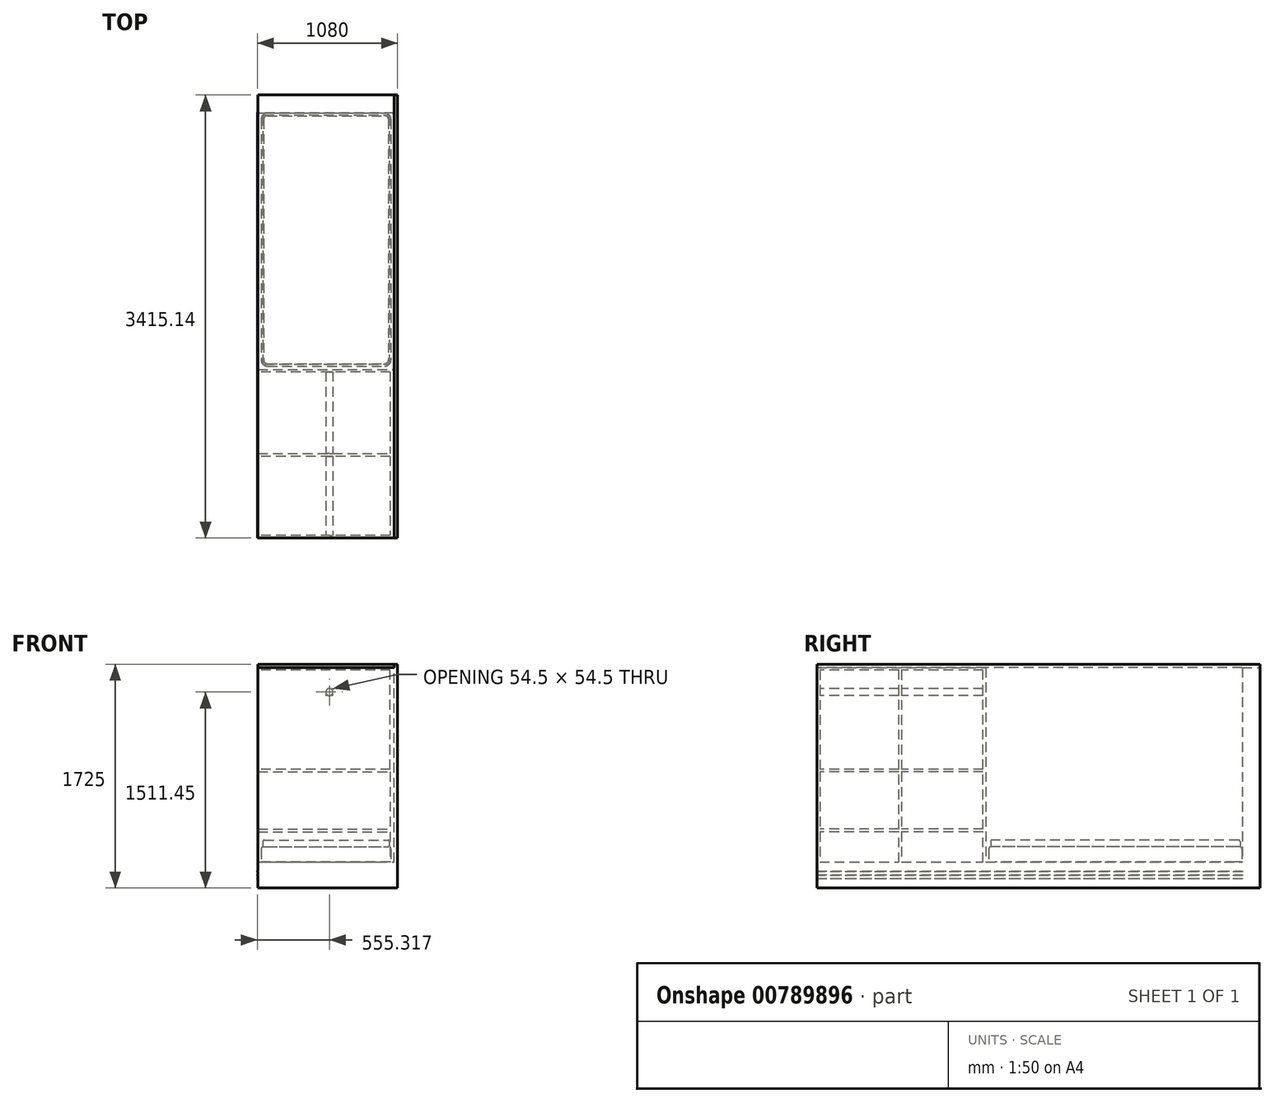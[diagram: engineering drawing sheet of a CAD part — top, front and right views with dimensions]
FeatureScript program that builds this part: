
annotation { "Feature Type Name" : "Feature", "Feature Type Description" : "" }
export const myFeature = defineFeature(function(context is Context, id is Id, definition is map)
    precondition{}
    {
        {
            var Q0;
            Q0=qCreatedBy(makeId("Top.planeOp"),FACE);
            var sketch = newSketch(context, id + "F0", { "sketchPlane" : qUnion([Q0])});
            skLineSegment(sketch, "E0.bottom", {"start": v(0, 0) * mm, "end": v(1050, 0) * mm});
            skLineSegment(sketch, "E0.top", {"start": v(0, 2000) * mm, "end": v(1050, 2000) * mm});
            skLineSegment(sketch, "E0.left", {"start": v(0, 0) * mm, "end": v(0, 2000) * mm});
            skLineSegment(sketch, "E0.right", {"start": v(1050, 0) * mm, "end": v(1050, 2000) * mm});
            skSolve(sketch);
        }
        {
            var Q0;
            Q0 = qSketchRegion(id + "F0", true);
            extrude(context, id + "F1", {"entities" : qUnion([Q0]), "depth" : 200 * mm, "offsetDistance" : 25 * mm});
        }
        {
            var Q0;
            Q0=makeQuery(id+"F1.opExtrude","SWEPT_EDGE",EDGE,{"disambiguationData":[OSD([sQuery(id+"F0.wireOp",EDGE,"E0.top"),sQuery(id+"F0.wireOp",EDGE,"E0.right")])]});
            var Q1;
            Q1=makeQuery(id+"F1.opExtrude","SWEPT_EDGE",EDGE,{"disambiguationData":[OSD([sQuery(id+"F0.wireOp",EDGE,"E0.top"),sQuery(id+"F0.wireOp",EDGE,"E0.left")])]});
            chamfer(context, id + "F2", {"entities" : qUnion([Q0, Q1]), "width" : 20 * mm, "tangentPropagation" : true});
        }
        {
            var Q0;
            Q0=makeQuery(id+"F1.opExtrude","CAP_FACE",FACE,{"disambiguationData":[OSD([sQuery(id+"F0.wireOp",EDGE,"E0.bottom"),sQuery(id+"F0.wireOp",EDGE,"E0.top"),sQuery(id+"F0.wireOp",EDGE,"E0.left"),sQuery(id+"F0.wireOp",EDGE,"E0.right")])],"isStart":false});
            var sketch = newSketch(context, id + "F3", { "sketchPlane" : qUnion([Q0])});
            skLineSegment(sketch, "E1.bottom", {"start": v(24.14, 1975.86) * mm, "end": v(1025.86, 1975.86) * mm});
            skLineSegment(sketch, "E1.top", {"start": v(24.14, 24.14) * mm, "end": v(1025.86, 24.14) * mm});
            skLineSegment(sketch, "E1.left", {"start": v(24.14, 1975.86) * mm, "end": v(24.14, 24.14) * mm});
            skLineSegment(sketch, "E1.right", {"start": v(1025.86, 1975.86) * mm, "end": v(1025.86, 24.14) * mm});
            skSolve(sketch);
        }
        {
            var Q0;
            Q0 = qSketchRegion(id + "F3", true);
            extrude(context, id + "F4", {"entities" : qUnion([Q0]), "operationType" : NewBodyOperationType.ADD, "depth" : 120 * mm, "offsetDistance" : 25 * mm});
        }
        {
            var Q0;
            Q0=makeQuery(id+"F4.opExtrude","SWEPT_EDGE",EDGE,{"disambiguationData":[OSD([sQuery(id+"F3.wireOp",EDGE,"E1.top"),sQuery(id+"F3.wireOp",EDGE,"E1.right")])]});
            var Q1;
            Q1=makeQuery(id+"F4.opExtrude","SWEPT_EDGE",EDGE,{"disambiguationData":[OSD([sQuery(id+"F3.wireOp",EDGE,"E1.bottom"),sQuery(id+"F3.wireOp",EDGE,"E1.right")])]});
            var Q2;
            Q2=makeQuery(id+"F4.opExtrude","SWEPT_EDGE",EDGE,{"disambiguationData":[OSD([sQuery(id+"F3.wireOp",EDGE,"E1.bottom"),sQuery(id+"F3.wireOp",EDGE,"E1.left")])]});
            var Q3;
            Q3=makeQuery(id+"F4.opExtrude","SWEPT_EDGE",EDGE,{"disambiguationData":[OSD([sQuery(id+"F3.wireOp",EDGE,"E1.top"),sQuery(id+"F3.wireOp",EDGE,"E1.left")])]});
            fillet(context, id + "F5", {"entities" : qUnion([Q0, Q1, Q2, Q3]), "radius" : 48.28 * mm, "tangentPropagation" : true, "allowEdgeOverflow" : false});
        }
        {
            var Q0;
            Q0=makeQuery(id+"F4.opExtrude","CAP_FACE",FACE,{"disambiguationData":[OSD([sQuery(id+"F3.wireOp",EDGE,"E1.bottom"),sQuery(id+"F3.wireOp",EDGE,"E1.top"),sQuery(id+"F3.wireOp",EDGE,"E1.left"),sQuery(id+"F3.wireOp",EDGE,"E1.right")])],"isStart":false});
            fillet(context, id + "F6", {"entities" : qUnion([Q0]), "radius" : 20 * mm, "tangentPropagation" : true, "allowEdgeOverflow" : false});
        }
        {
            var Q0;
            Q0=makeQuery(id+"F4.opExtrude","CAP_FACE",FACE,{"disambiguationData":[OSD([sQuery(id+"F3.wireOp",EDGE,"E1.bottom"),sQuery(id+"F3.wireOp",EDGE,"E1.top"),sQuery(id+"F3.wireOp",EDGE,"E1.left"),sQuery(id+"F3.wireOp",EDGE,"E1.right")])],"isStart":false});
            var sketch = newSketch(context, id + "F7", { "sketchPlane" : qUnion([Q0])});
            skLineSegment(sketch, "E2.bottom", {"start": v(38.28, 1961.73) * mm, "end": v(1011.68, 1961.73) * mm});
            skLineSegment(sketch, "E2.top", {"start": v(38.28, 38.25) * mm, "end": v(1011.68, 38.25) * mm});
            skLineSegment(sketch, "E2.left", {"start": v(38.28, 1961.73) * mm, "end": v(38.28, 38.25) * mm});
            skLineSegment(sketch, "E2.right", {"start": v(1011.68, 1961.73) * mm, "end": v(1011.68, 38.25) * mm});
            skSolve(sketch);
        }
        {
            var Q0;
            Q0 = qSketchRegion(id + "F7", true);
            extrude(context, id + "F8", {"entities" : qUnion([Q0]), "operationType" : NewBodyOperationType.ADD, "depth" : 50 * mm, "offsetDistance" : 25 * mm});
        }
        {
            var Q0;
            Q0=makeQuery(id+"F8.opExtrude","SWEPT_EDGE",EDGE,{"disambiguationData":[OSD([sQuery(id+"F7.wireOp",EDGE,"E2.top"),sQuery(id+"F7.wireOp",EDGE,"E2.right")])]});
            var Q1;
            Q1=makeQuery(id+"F8.opExtrude","SWEPT_EDGE",EDGE,{"disambiguationData":[OSD([sQuery(id+"F7.wireOp",EDGE,"E2.bottom"),sQuery(id+"F7.wireOp",EDGE,"E2.right")])]});
            var Q2;
            Q2=makeQuery(id+"F8.opExtrude","SWEPT_EDGE",EDGE,{"disambiguationData":[OSD([sQuery(id+"F7.wireOp",EDGE,"E2.bottom"),sQuery(id+"F7.wireOp",EDGE,"E2.left")])]});
            var Q3;
            Q3=makeQuery(id+"F8.opExtrude","SWEPT_EDGE",EDGE,{"disambiguationData":[OSD([sQuery(id+"F7.wireOp",EDGE,"E2.top"),sQuery(id+"F7.wireOp",EDGE,"E2.left")])]});
            fillet(context, id + "F9", {"entities" : qUnion([Q0, Q1, Q2, Q3]), "radius" : 10 * mm, "tangentPropagation" : true, "allowEdgeOverflow" : false});
        }
        {
            var Q0;
            Q0=makeQuery(id+"F8.opExtrude","CAP_FACE",FACE,{"disambiguationData":[OSD([sQuery(id+"F7.wireOp",EDGE,"E2.bottom"),sQuery(id+"F7.wireOp",EDGE,"E2.top"),sQuery(id+"F7.wireOp",EDGE,"E2.left"),sQuery(id+"F7.wireOp",EDGE,"E2.right")])],"isStart":false});
            fillet(context, id + "F10", {"entities" : qUnion([Q0]), "radius" : 10 * mm, "tangentPropagation" : true, "allowEdgeOverflow" : false});
        }
        {
            var Q0;
            Q0=makeQuery(id+"F1.opExtrude","SWEPT_FACE",FACE,{"disambiguationData":[OSD([sQuery(id+"F0.wireOp",EDGE,"E0.left")])]});
            var sketch = newSketch(context, id + "F11", { "sketchPlane" : qUnion([Q0])});
            skLineSegment(sketch, "E3", {"start": v(-1980, 0) * mm, "end": v(-1980, 70) * mm});
            skLineSegment(sketch, "E4", {"start": v(-1980, 70) * mm, "end": v(-20, 70) * mm});
            skLineSegment(sketch, "E5", {"start": v(-20, 200) * mm, "end": v(-20, 130) * mm});
            skLineSegment(sketch, "E6", {"start": v(-20, 130) * mm, "end": v(-1980, 130) * mm});
            skLineSegment(sketch, "E7", {"start": v(-1980, 130) * mm, "end": v(-1980, 124.9) * mm});
            skLineSegment(sketch, "E8", {"start": v(-1980, 70) * mm, "end": v(-1980, 130) * mm});
            skLineSegment(sketch, "E9", {"start": v(-1980, 100) * mm, "end": v(-20, 100) * mm});
            skLineSegment(sketch, "E10", {"start": v(-20, 100) * mm, "end": v(-20, 103) * mm});
            skLineSegment(sketch, "E11", {"start": v(-20, 103) * mm, "end": v(-1980, 103) * mm});
            skLineSegment(sketch, "E12", {"start": v(-1980, 100) * mm, "end": v(-1980, 97) * mm});
            skLineSegment(sketch, "E13", {"start": v(-1980, 97) * mm, "end": v(-20, 97) * mm});
            skLineSegment(sketch, "E14", {"start": v(-20, 97) * mm, "end": v(-20, 100) * mm});
            skLineSegment(sketch, "E15", {"start": v(-1980, 130) * mm, "end": v(-1980, 125) * mm});
            skLineSegment(sketch, "E16", {"start": v(-1980, 125) * mm, "end": v(-20, 125) * mm});
            skLineSegment(sketch, "E17", {"start": v(-20, 125) * mm, "end": v(-20, 130) * mm});
            skLineSegment(sketch, "E18", {"start": v(-20, 70) * mm, "end": v(-20, 75) * mm});
            skLineSegment(sketch, "E19", {"start": v(-20, 75) * mm, "end": v(-1980, 75) * mm});
            skLineSegment(sketch, "E20", {"start": v(-1980, 75) * mm, "end": v(-1980, 70) * mm});
            skSolve(sketch);
        }
        {
            var Q0;
            Q0 = qSketchRegion(id + "F11", true);
            extrude(context, id + "F12", {"entities" : qUnion([Q0]), "operationType" : NewBodyOperationType.ADD, "depth" : 5 * mm, "offsetDistance" : 25 * mm});
        }
        {
            var Q0;
            Q0=qCreatedBy(makeId("Top.planeOp"),FACE);
            var sketch = newSketch(context, id + "F13", { "sketchPlane" : qUnion([Q0])});
            skLineSegment(sketch, "E21.bottom", {"start": v(0, 0) * mm, "end": v(1050, 0) * mm});
            skLineSegment(sketch, "E21.top", {"start": v(0, -1300) * mm, "end": v(1050, -1300) * mm});
            skLineSegment(sketch, "E21.left", {"start": v(0, 0) * mm, "end": v(0, -1300) * mm});
            skLineSegment(sketch, "E21.right", {"start": v(1050, 0) * mm, "end": v(1050, -1300) * mm});
            skSolve(sketch);
        }
        {
            var Q0;
            Q0=makeQuery(id+"F13.imprint","IMPRINT",FACE,{"disambiguationData":[TD([[makeQuery(id+"F13.imprint","IMPRINT",EDGE,{"derivedFrom":sQuery(id+"F13.wireOp",EDGE,"E21.bottom")}),-1.0]])]});
            extrude(context, id + "F14", {"entities" : qUnion([Q0]), "operationType" : NewBodyOperationType.ADD, "depth" : 200 * mm, "offsetDistance" : 25 * mm});
        }
        {
            var Q0;
            Q0=makeQuery(id+"F14.boolean.opBoolean","MERGE",FACE,{"derivedFrom":[makeQuery(id+"F1.opExtrude","CAP_FACE",FACE,{"disambiguationData":[OSD([sQuery(id+"F0.wireOp",EDGE,"E0.bottom"),sQuery(id+"F0.wireOp",EDGE,"E0.top"),sQuery(id+"F0.wireOp",EDGE,"E0.left"),sQuery(id+"F0.wireOp",EDGE,"E0.right")])],"isStart":false}),makeQuery(id+"F14.opExtrude","CAP_FACE",FACE,{"disambiguationData":[OSD([sQuery(id+"F13.wireOp",EDGE,"E21.bottom"),sQuery(id+"F13.wireOp",EDGE,"E21.top"),sQuery(id+"F13.wireOp",EDGE,"E21.left"),sQuery(id+"F13.wireOp",EDGE,"E21.right")])],"isStart":false})]});
            var sketch = newSketch(context, id + "F15", { "sketchPlane" : qUnion([Q0])});
            skLineSegment(sketch, "E22.bottom", {"start": v(0, 0) * mm, "end": v(1050, 0) * mm});
            skLineSegment(sketch, "E22.top", {"start": v(0, -1300) * mm, "end": v(1050, -1300) * mm});
            skLineSegment(sketch, "E22.left", {"start": v(0, 0) * mm, "end": v(0, -1300) * mm});
            skLineSegment(sketch, "E22.right", {"start": v(1050, 0) * mm, "end": v(1050, -1300) * mm});
            skSolve(sketch);
        }
        {
            var Q0;
            Q0 = qSketchRegion(id + "F15", true);
            extrude(context, id + "F16", {"entities" : qUnion([Q0]), "operationType" : NewBodyOperationType.ADD, "depth" : 1500 * mm, "offsetDistance" : 25 * mm});
        }
        {
            var Q0;
            Q0=makeQuery(id+"F16.boolean.opBoolean","MERGE",FACE,{"derivedFrom":[makeQuery(id+"F14.boolean.opBoolean","MERGE",FACE,{"derivedFrom":[makeQuery(id+"F1.opExtrude","SWEPT_FACE",FACE,{"disambiguationData":[OSD([sQuery(id+"F0.wireOp",EDGE,"E0.left")])]}),makeQuery(id+"F14.opExtrude","SWEPT_FACE",FACE,{"disambiguationData":[OSD([sQuery(id+"F13.wireOp",EDGE,"E21.left")])]})]}),makeQuery(id+"F16.opExtrude","SWEPT_FACE",FACE,{"disambiguationData":[OSD([sQuery(id+"F15.wireOp",EDGE,"E22.left")])]})]});
            var sketch = newSketch(context, id + "F17", { "sketchPlane" : qUnion([Q0])});
            skLineSegment(sketch, "E23", {"start": v(0, 1700) * mm, "end": v(20, 1700) * mm});
            skLineSegment(sketch, "E24", {"start": v(20, 1700) * mm, "end": v(20, 1680) * mm});
            skLineSegment(sketch, "E25", {"start": v(20, 1680) * mm, "end": v(1300, 1680) * mm});
            skLineSegment(sketch, "E26", {"start": v(1300, 1680) * mm, "end": v(1280, 1680) * mm});
            skLineSegment(sketch, "E27", {"start": v(1280, 1680) * mm, "end": v(1280, 200) * mm});
            skLineSegment(sketch, "E28", {"start": v(1280, 200) * mm, "end": v(20, 200) * mm});
            skLineSegment(sketch, "E29", {"start": v(20, 200) * mm, "end": v(20, 1680) * mm});
            skLineSegment(sketch, "E30", {"start": v(660, 1680) * mm, "end": v(660, 200) * mm});
            skLineSegment(sketch, "E31", {"start": v(660, 200) * mm, "end": v(670, 200) * mm});
            skLineSegment(sketch, "E32", {"start": v(670, 200) * mm, "end": v(670, 1680) * mm});
            skLineSegment(sketch, "E33", {"start": v(670, 1680) * mm, "end": v(650, 1680) * mm});
            skLineSegment(sketch, "E34", {"start": v(650, 1680) * mm, "end": v(650, 200) * mm});
            skSolve(sketch);
        }
        {
            var Q0;
            {var subQ0=sQuery(id+"F17.wireOp",EDGE,"E27");Q0=makeQuery(id+"F17.imprint","IMPRINT",FACE,{"disambiguationData":[TD([[makeQuery(id+"F17.imprint","IMPRINT",EDGE,{"derivedFrom":subQ0}),-1.0]])]});}
            var Q1;
            {var subQ0=sQuery(id+"F17.wireOp",EDGE,"E29");Q1=makeQuery(id+"F17.imprint","IMPRINT",FACE,{"disambiguationData":[TD([[makeQuery(id+"F17.imprint","IMPRINT",EDGE,{"derivedFrom":subQ0}),-1.0]])]});}
            extrude(context, id + "F18", {"entities" : qUnion([Q0, Q1]), "operationType" : NewBodyOperationType.REMOVE, "oppositeDirection" : true, "depth" : 1019 * mm, "offsetDistance" : 25 * mm});
        }
        {
            var Q0;
            Q0=makeQuery(id+"F16.boolean.opBoolean","MERGE",FACE,{"derivedFrom":[makeQuery(id+"F14.boolean.opBoolean","MERGE",FACE,{"derivedFrom":[makeQuery(id+"F1.opExtrude","SWEPT_FACE",FACE,{"disambiguationData":[OSD([sQuery(id+"F0.wireOp",EDGE,"E0.left")])]}),makeQuery(id+"F14.opExtrude","SWEPT_FACE",FACE,{"disambiguationData":[OSD([sQuery(id+"F13.wireOp",EDGE,"E21.left")])]})]}),makeQuery(id+"F16.opExtrude","SWEPT_FACE",FACE,{"disambiguationData":[OSD([sQuery(id+"F15.wireOp",EDGE,"E22.left")])]})]});
            var sketch = newSketch(context, id + "F19", { "sketchPlane" : qUnion([Q0])});
            skLineSegment(sketch, "E35", {"start": v(-20, 130) * mm, "end": v(1300, 130) * mm});
            skLineSegment(sketch, "E36", {"start": v(-20, 125) * mm, "end": v(1300, 125) * mm});
            skLineSegment(sketch, "E37", {"start": v(1300, 125) * mm, "end": v(1300, 130) * mm});
            skLineSegment(sketch, "E38.bottom", {"start": v(-20, 103) * mm, "end": v(1300, 103) * mm});
            skLineSegment(sketch, "E38.top", {"start": v(-20, 97) * mm, "end": v(1300, 97) * mm});
            skLineSegment(sketch, "E38.left", {"start": v(-20, 103) * mm, "end": v(-20, 97) * mm});
            skLineSegment(sketch, "E38.right", {"start": v(1300, 103) * mm, "end": v(1300, 97) * mm});
            skLineSegment(sketch, "E39.bottom", {"start": v(-20, 75) * mm, "end": v(1300, 75) * mm});
            skLineSegment(sketch, "E39.top", {"start": v(-20, 70) * mm, "end": v(1300, 70) * mm});
            skLineSegment(sketch, "E39.left", {"start": v(-20, 75) * mm, "end": v(-20, 70) * mm});
            skLineSegment(sketch, "E39.right", {"start": v(1300, 75) * mm, "end": v(1300, 70) * mm});
            skLineSegment(sketch, "E40", {"start": v(-20, 130) * mm, "end": v(-20, 125) * mm});
            skSolve(sketch);
        }
        {
            var Q0;
            Q0 = qSketchRegion(id + "F19", true);
            extrude(context, id + "F20", {"entities" : qUnion([Q0]), "operationType" : NewBodyOperationType.ADD, "depth" : 5 * mm, "offsetDistance" : 25 * mm});
        }
        {
            var Q0;
            Q0=qCreatedBy(makeId("Top.planeOp"),FACE);
            var sketch = newSketch(context, id + "F21", { "sketchPlane" : qUnion([Q0])});
            skLineSegment(sketch, "E41.bottom", {"start": v(1061.66, 1978.14) * mm, "end": v(0, 1978.14) * mm});
            skLineSegment(sketch, "E41.top", {"start": v(1061.66, 3200.14) * mm, "end": v(0, 3200.14) * mm});
            skLineSegment(sketch, "E41.left", {"start": v(1061.66, 1978.14) * mm, "end": v(1061.66, 3200.14) * mm});
            skLineSegment(sketch, "E41.right", {"start": v(0, 1978.14) * mm, "end": v(0, 3200.14) * mm});
            skSolve(sketch);
        }
        {
            var Q0;
            Q0=makeQuery(id+"F21.imprint","IMPRINT",FACE,{"disambiguationData":[TD([[makeQuery(id+"F21.imprint","IMPRINT",EDGE,{"derivedFrom":sQuery(id+"F21.wireOp",EDGE,"E41.bottom")}),-1.0]])]});
            extrude(context, id + "F22", {"entities" : qUnion([Q0]), "operationType" : NewBodyOperationType.ADD, "depth" : 1700 * mm, "offsetDistance" : 25 * mm});
        }
        {
            var Q0;
            Q0=makeQuery(id+"F22.opExtrude","SWEPT_FACE",FACE,{"disambiguationData":[OSD([sQuery(id+"F21.wireOp",EDGE,"E41.top")])]});
            var sketch = newSketch(context, id + "F23", { "sketchPlane" : qUnion([Q0])});
            skLineSegment(sketch, "E42.bottom", {"start": v(-287.27, 0) * mm, "end": v(-322.94, 0) * mm});
            skLineSegment(sketch, "E42.top", {"start": v(-287.27, 1700) * mm, "end": v(-322.94, 1700) * mm});
            skLineSegment(sketch, "E42.left", {"start": v(-287.27, 0) * mm, "end": v(-287.27, 1700) * mm});
            skLineSegment(sketch, "E42.right", {"start": v(-322.94, 0) * mm, "end": v(-322.94, 1700) * mm});
            skLineSegment(sketch, "E43.bottom", {"start": v(-675.83, 1700) * mm, "end": v(-715.48, 1700) * mm});
            skLineSegment(sketch, "E43.top", {"start": v(-675.83, 0) * mm, "end": v(-715.48, 0) * mm});
            skLineSegment(sketch, "E43.left", {"start": v(-675.83, 1700) * mm, "end": v(-675.83, 0) * mm});
            skLineSegment(sketch, "E43.right", {"start": v(-715.48, 1700) * mm, "end": v(-715.48, 0) * mm});
            skSolve(sketch);
        }
        {
            var Q0;
            Q0 = qSketchRegion(id + "F23", true);
            extrude(context, id + "F24", {"entities" : qUnion([Q0]), "operationType" : NewBodyOperationType.ADD, "depth" : 95 * mm, "offsetDistance" : 25 * mm});
        }
        {
            var Q0;
            Q0=makeQuery(id+"F24.opExtrude","SWEPT_FACE",FACE,{"disambiguationData":[OSD([sQuery(id+"F23.wireOp",EDGE,"E43.left")])]});
            var sketch = newSketch(context, id + "F25", { "sketchPlane" : qUnion([Q0])});
            skCircle(sketch, "E44", {"center": v(-3252.89, 135.2) * mm, "radius": 17.68 * mm});
            skCircle(sketch, "E45", {"center": v(-3254.5, 222.68) * mm, "radius": 26.5 * mm});
            skCircle(sketch, "E46", {"center": v(-3248.26, 335.37) * mm, "radius": 28.5 * mm});
            skCircle(sketch, "E47", {"center": v(-3249.73, 494.15) * mm, "radius": 25.46 * mm});
            skCircle(sketch, "E48", {"center": v(-3252.81, 419.3) * mm, "radius": 22.12 * mm});
            skCircle(sketch, "E49", {"center": v(-3253.4, 580.16) * mm, "radius": 26.8 * mm});
            skCircle(sketch, "E50", {"center": v(-3251.75, 678.68) * mm, "radius": 26.84 * mm});
            skCircle(sketch, "E51", {"center": v(-3255.38, 785.06) * mm, "radius": 29.86 * mm});
            skCircle(sketch, "E52", {"center": v(-3254.4, 915.8) * mm, "radius": 34.52 * mm});
            skCircle(sketch, "E53", {"center": v(-3239.5, 1025.25) * mm, "radius": 18.48 * mm});
            skCircle(sketch, "E54", {"center": v(-3245.4, 1183.77) * mm, "radius": 24.44 * mm});
            skCircle(sketch, "E55", {"center": v(-3251.76, 1320.89) * mm, "radius": 26.5 * mm});
            skCircle(sketch, "E56", {"center": v(-3255.53, 1433.7) * mm, "radius": 18.37 * mm});
            skCircle(sketch, "E57", {"center": v(-3246.57, 1505.49) * mm, "radius": 19.14 * mm});
            skCircle(sketch, "E58", {"center": v(-3261.74, 1574.56) * mm, "radius": 20 * mm});
            skSolve(sketch);
        }
        {
            var Q0;
            Q0 = qSketchRegion(id + "F25", true);
            extrude(context, id + "F26", {"entities" : qUnion([Q0]), "operationType" : NewBodyOperationType.ADD, "depth" : 365 * mm, "offsetDistance" : 25 * mm});
        }
        {
            var Q0;
            Q0=makeQuery(id+"F24.boolean.opBoolean","MERGE",FACE,{"derivedFrom":[makeQuery(id+"F22.opExtrude","CAP_FACE",FACE,{"disambiguationData":[OSD([sQuery(id+"F21.wireOp",EDGE,"E41.bottom"),sQuery(id+"F21.wireOp",EDGE,"E41.top"),sQuery(id+"F21.wireOp",EDGE,"E41.left"),sQuery(id+"F21.wireOp",EDGE,"E41.right")])],"isStart":false}),makeQuery(id+"F24.opExtrude","SWEPT_FACE",FACE,{"disambiguationData":[OSD([sQuery(id+"F23.wireOp",EDGE,"E42.top")])]}),makeQuery(id+"F24.opExtrude","SWEPT_FACE",FACE,{"disambiguationData":[OSD([sQuery(id+"F23.wireOp",EDGE,"E43.bottom")])]})]});
            var sketch = newSketch(context, id + "F27", { "sketchPlane" : qUnion([Q0])});
            skLineSegment(sketch, "E59.bottom", {"start": v(0, 3200.14) * mm, "end": v(1048.55, 3200.14) * mm});
            skLineSegment(sketch, "E59.top", {"start": v(0, -1299.65) * mm, "end": v(1048.55, -1299.65) * mm});
            skLineSegment(sketch, "E59.left", {"start": v(0, 3200.14) * mm, "end": v(0, -1299.65) * mm});
            skLineSegment(sketch, "E59.right", {"start": v(1048.55, 3200.14) * mm, "end": v(1048.55, -1299.65) * mm});
            skSolve(sketch);
        }
        {
            var Q0;
            Q0 = qSketchRegion(id + "F27", true);
            extrude(context, id + "F28", {"entities" : qUnion([Q0]), "operationType" : NewBodyOperationType.ADD, "depth" : 25 * mm, "offsetDistance" : 25 * mm});
        }
        {
            var Q0;
            Q0=makeQuery(id+"F16.boolean.opBoolean","MERGE",FACE,{"derivedFrom":[makeQuery(id+"F14.boolean.opBoolean","MERGE",FACE,{"derivedFrom":[makeQuery(id+"F1.opExtrude","SWEPT_FACE",FACE,{"disambiguationData":[OSD([sQuery(id+"F0.wireOp",EDGE,"E0.right")])]}),makeQuery(id+"F14.opExtrude","SWEPT_FACE",FACE,{"disambiguationData":[OSD([sQuery(id+"F13.wireOp",EDGE,"E21.right")])]})]}),makeQuery(id+"F16.opExtrude","SWEPT_FACE",FACE,{"disambiguationData":[OSD([sQuery(id+"F15.wireOp",EDGE,"E22.right")])]})]});
            var sketch = newSketch(context, id + "F29", { "sketchPlane" : qUnion([Q0])});
            skLineSegment(sketch, "E60.bottom", {"start": v(-1300, 0) * mm, "end": v(3199.94, 0) * mm});
            skLineSegment(sketch, "E60.top", {"start": v(-1300, 1724.51) * mm, "end": v(3199.94, 1724.51) * mm});
            skLineSegment(sketch, "E60.left", {"start": v(-1300, 0) * mm, "end": v(-1300, 1724.51) * mm});
            skLineSegment(sketch, "E60.right", {"start": v(3199.94, 0) * mm, "end": v(3199.94, 1724.51) * mm});
            skSolve(sketch);
        }
        {
            var Q0;
            Q0 = qSketchRegion(id + "F29", true);
            extrude(context, id + "F30", {"entities" : qUnion([Q0]), "operationType" : NewBodyOperationType.ADD, "depth" : 25 * mm, "offsetDistance" : 25 * mm});
        }
        {
            var Q0;
            Q0=makeQuery(id+"F24.opExtrude","CAP_FACE",FACE,{"disambiguationData":[OSD([sQuery(id+"F23.wireOp",EDGE,"E42.bottom"),sQuery(id+"F23.wireOp",EDGE,"E42.top"),sQuery(id+"F23.wireOp",EDGE,"E42.left"),sQuery(id+"F23.wireOp",EDGE,"E42.right")])],"isStart":false});
            var sketch = newSketch(context, id + "F31", { "sketchPlane" : qUnion([Q0])});
            skLineSegment(sketch, "E61.bottom", {"start": v(-1123.49, 1753.47) * mm, "end": v(132.5, 1753.47) * mm});
            skLineSegment(sketch, "E61.top", {"start": v(-1123.49, -94.46) * mm, "end": v(132.5, -94.46) * mm});
            skLineSegment(sketch, "E61.left", {"start": v(-1123.49, 1753.47) * mm, "end": v(-1123.49, -94.46) * mm});
            skLineSegment(sketch, "E61.right", {"start": v(132.5, 1753.47) * mm, "end": v(132.5, -94.46) * mm});
            skSolve(sketch);
        }
        {
            var Q0;
            Q0 = qSketchRegion(id + "F31", true);
            extrude(context, id + "F32", {"entities" : qUnion([Q0]), "operationType" : NewBodyOperationType.REMOVE, "oppositeDirection" : true, "depth" : 1180 * mm, "offsetDistance" : 25 * mm});
        }
        {
            var Q0;
            Q0=makeQuery(id+"F18.boolean.opBoolean","COPY",FACE,{"derivedFrom":makeQuery(id+"F18.opExtrude","SWEPT_FACE",FACE,{"disambiguationData":[OSD([sQuery(id+"F17.wireOp",EDGE,"E27")])]})});
            var sketch = newSketch(context, id + "F33", { "sketchPlane" : qUnion([Q0])});
            skCircle(sketch, "E62", {"center": v(-550.32, 1511.45) * mm, "radius": 27.25 * mm});
            skSolve(sketch);
        }
        {
            var Q0;
            Q0 = qSketchRegion(id + "F33", true);
            extrude(context, id + "F34", {"entities" : qUnion([Q0]), "operationType" : NewBodyOperationType.ADD, "depth" : 1280 * mm, "offsetDistance" : 25 * mm});
        }
        {
            var Q0;
            Q0=makeQuery(id+"F18.boolean.opBoolean","COPY",FACE,{"derivedFrom":makeQuery(id+"F18.opExtrude","SWEPT_FACE",FACE,{"disambiguationData":[OSD([sQuery(id+"F17.wireOp",EDGE,"E27")])]})});
            var sketch = newSketch(context, id + "F35", { "sketchPlane" : qUnion([Q0])});
            skLineSegment(sketch, "E63.bottom", {"start": v(-1019, 432.38) * mm, "end": v(0, 432.38) * mm});
            skLineSegment(sketch, "E63.top", {"start": v(-1019, 453.94) * mm, "end": v(0, 453.94) * mm});
            skLineSegment(sketch, "E63.left", {"start": v(-1019, 432.38) * mm, "end": v(-1019, 453.94) * mm});
            skLineSegment(sketch, "E63.right", {"start": v(0, 432.38) * mm, "end": v(0, 453.94) * mm});
            skSolve(sketch);
        }
        {
            var Q0;
            Q0 = qSketchRegion(id + "F35", true);
            extrude(context, id + "F36", {"entities" : qUnion([Q0]), "operationType" : NewBodyOperationType.ADD, "depth" : 1272 * mm, "offsetDistance" : 25 * mm});
        }
        {
            var Q0;
            {var subQ0=sQuery(id+"F17.wireOp",EDGE,"E27");Q0=makeQuery(id+"F36.boolean.opBoolean","SPLIT",FACE,{"disambiguationData":[TD([makeQuery(id+"F34.opExtrude","SWEPT_FACE",FACE,{"disambiguationData":[OSD([sQuery(id+"F33.wireOp",EDGE,"E62")])]})])],"derivedFrom":makeQuery(id+"F18.boolean.opBoolean","COPY",FACE,{"derivedFrom":makeQuery(id+"F18.opExtrude","SWEPT_FACE",FACE,{"disambiguationData":[OSD([subQ0])]})})});}
            var sketch = newSketch(context, id + "F37", { "sketchPlane" : qUnion([Q0])});
            skLineSegment(sketch, "E64.bottom", {"start": v(-1019, 916.21) * mm, "end": v(0, 916.21) * mm});
            skLineSegment(sketch, "E64.top", {"start": v(-1019, 895.25) * mm, "end": v(0, 895.25) * mm});
            skLineSegment(sketch, "E64.left", {"start": v(-1019, 916.21) * mm, "end": v(-1019, 895.25) * mm});
            skLineSegment(sketch, "E64.right", {"start": v(0, 916.21) * mm, "end": v(0, 895.25) * mm});
            skSolve(sketch);
        }
        {
            var Q0;
            Q0 = qSketchRegion(id + "F37", true);
            extrude(context, id + "F38", {"entities" : qUnion([Q0]), "operationType" : NewBodyOperationType.ADD, "depth" : 1280 * mm, "offsetDistance" : 25 * mm});
        }
    });
